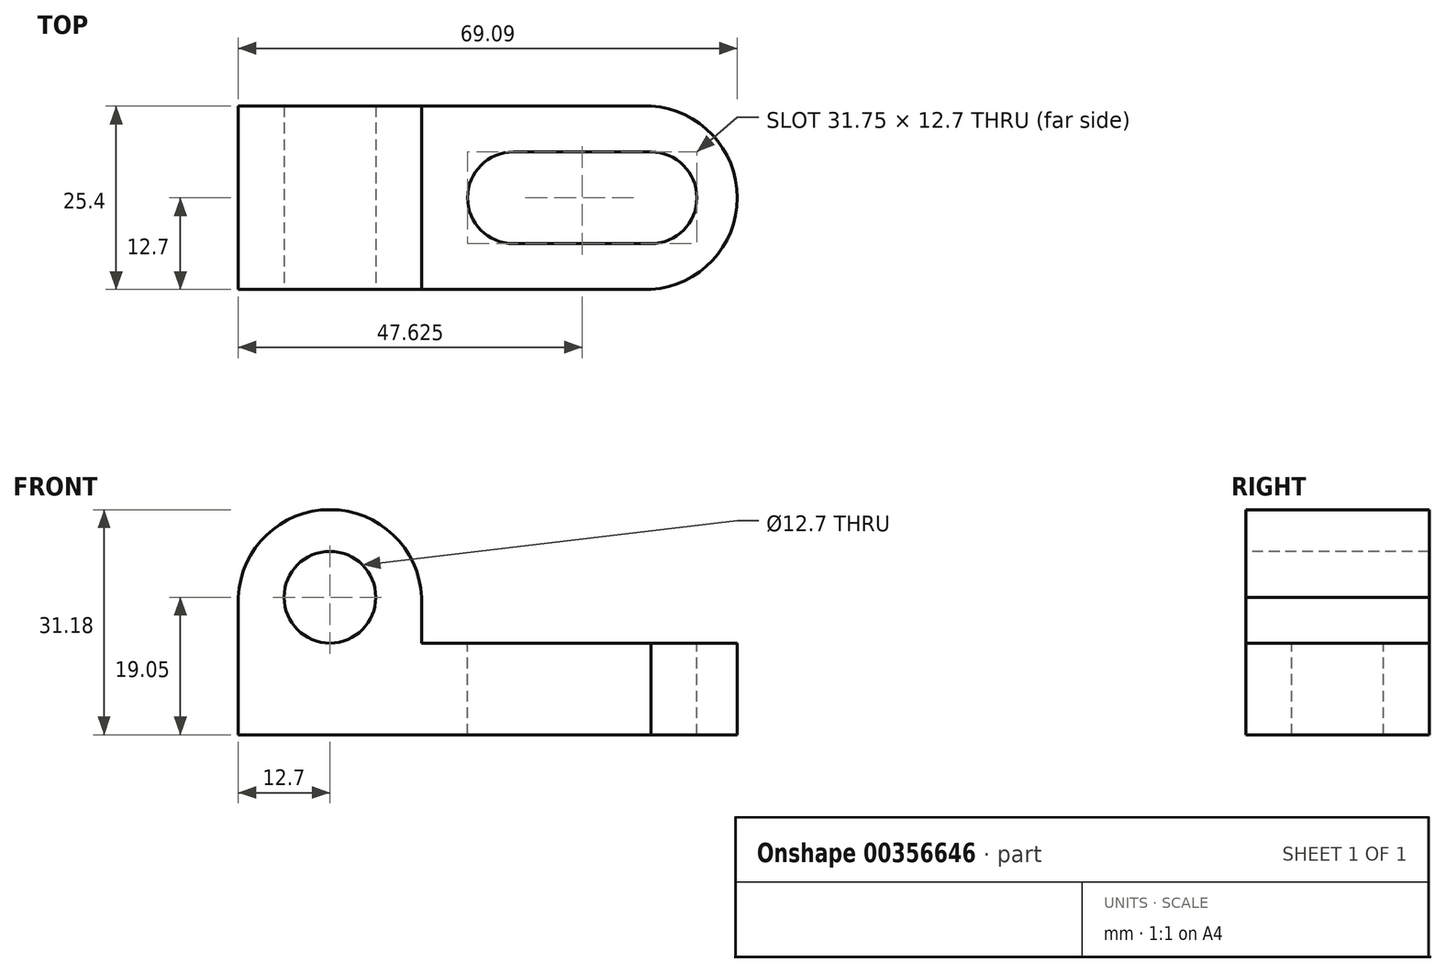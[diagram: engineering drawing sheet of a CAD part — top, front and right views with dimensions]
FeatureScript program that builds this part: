
annotation { "Feature Type Name" : "Feature", "Feature Type Description" : "" }
export const myFeature = defineFeature(function(context is Context, id is Id, definition is map)
    precondition{}
    {
        {
            var Q0;
            Q0=qCreatedBy(makeId("Front.planeOp"),FACE);
            var sketch = newSketch(context, id + "F0", { "sketchPlane" : qUnion([Q0])});
            skLineSegment(sketch, "E0", {"start": v(0, 0) * mm, "end": v(69.85, 0) * mm});
            skLineSegment(sketch, "E1", {"start": v(69.85, 0) * mm, "end": v(69.85, 12.7) * mm});
            skLineSegment(sketch, "E2", {"start": v(69.85, 12.7) * mm, "end": v(25.4, 12.7) * mm});
            skLineSegment(sketch, "E3", {"start": v(25.4, 12.7) * mm, "end": v(25.4, 31.75) * mm});
            skLineSegment(sketch, "E4", {"start": v(25.4, 31.75) * mm, "end": v(0, 31.75) * mm});
            skLineSegment(sketch, "E5", {"start": v(0, 31.75) * mm, "end": v(0, 0) * mm});
            skSolve(sketch);
        }
        {
            var Q0;
            Q0=makeQuery(id+"F0.imprint","IMPRINT",FACE,{"disambiguationData":[TD([[makeQuery(id+"F0.imprint","IMPRINT",EDGE,{"derivedFrom":sQuery(id+"F0.wireOp",EDGE,"E0")}),1.0]])]});
            extrude(context, id + "F1", {"entities" : qUnion([Q0]), "depth" : 25.4 * mm});
        }
        {
            var Q0;
            Q0=makeQuery(id+"F1.opExtrude","CAP_FACE",FACE,{"disambiguationData":[OSD([sQuery(id+"F0.wireOp",EDGE,"E0"),sQuery(id+"F0.wireOp",EDGE,"E1"),sQuery(id+"F0.wireOp",EDGE,"E2"),sQuery(id+"F0.wireOp",EDGE,"E3"),sQuery(id+"F0.wireOp",EDGE,"E4"),sQuery(id+"F0.wireOp",EDGE,"E5")])],"isStart":false});
            var sketch = newSketch(context, id + "F2", { "sketchPlane" : qUnion([Q0])});
            skCircle(sketch, "E6", {"center": v(12.7, 19.05) * mm, "radius": 6.35 * mm});
            skArc(sketch, "E7", {"start": v(25.4, 19.05) * mm, "mid": v(12.7, 31.18) * mm, "end": v(0, 19.05) * mm});
            skSolve(sketch);
        }
        {
            var Q0;
            {var subQ0=sQuery(id+"F2.wireOp",EDGE,"E7");Q0=makeQuery(id+"F2.imprint","IMPRINT",FACE,{"disambiguationData":[TD([[makeQuery(id+"F2.imprint","IMPRINT",EDGE,{"derivedFrom":subQ0}),-1.0]])]});}
            var Q1;
            Q1=makeQuery(id+"F2.imprint","IMPRINT",FACE,{"disambiguationData":[TD([[makeQuery(id+"F2.imprint","IMPRINT",EDGE,{"derivedFrom":sQuery(id+"F2.wireOp",EDGE,"E6")}),1.0]])]});
            extrude(context, id + "F3", {"entities" : qUnion([Q0, Q1]), "operationType" : NewBodyOperationType.REMOVE, "oppositeDirection" : true, "depth" : 25.4 * mm});
        }
        {
            var Q0;
            Q0=makeQuery(id+"F1.opExtrude","SWEPT_FACE",FACE,{"disambiguationData":[OSD([sQuery(id+"F0.wireOp",EDGE,"E2")])]});
            var sketch = newSketch(context, id + "F4", { "sketchPlane" : qUnion([Q0])});
            skCircle(sketch, "E8", {"center": v(38.1, -12.7) * mm, "radius": 6.35 * mm});
            skCircle(sketch, "E9", {"center": v(57.15, -12.7) * mm, "radius": 6.35 * mm});
            skLineSegment(sketch, "E10", {"start": v(38.1, -6.35) * mm, "end": v(57.15, -6.35) * mm});
            skLineSegment(sketch, "E11", {"start": v(38.1, -19.05) * mm, "end": v(57.15, -19.05) * mm});
            skArc(sketch, "E12", {"start": v(57.15, -25.4) * mm, "mid": v(69.09, -12.7) * mm, "end": v(57.15, 0) * mm});
            skSolve(sketch);
        }
        {
            var Q0;
            {var subQ0=sQuery(id+"F4.wireOp",EDGE,"E8");var subQ1=makeQuery(id+"F4.imprint","INTERSECT",VERTEX,{"derivedFrom":[subQ0,sQuery(id+"F4.wireOp",EDGE,"E10")]});Q0=makeQuery(id+"F4.imprint","IMPRINT",FACE,{"disambiguationData":[TD([[makeQuery(id+"F4.imprint","IMPRINT",EDGE,{"disambiguationData":[TD([[subQ1,-1.0]])],"derivedFrom":subQ0}),1.0]])]});}
            var Q1;
            {var subQ0=sQuery(id+"F4.wireOp",EDGE,"E10");Q1=makeQuery(id+"F4.imprint","IMPRINT",FACE,{"disambiguationData":[TD([[makeQuery(id+"F4.imprint","IMPRINT",EDGE,{"derivedFrom":subQ0}),-1.0]])]});}
            var Q2;
            {var subQ0=sQuery(id+"F4.wireOp",EDGE,"E9");var subQ1=makeQuery(id+"F4.imprint","INTERSECT",VERTEX,{"derivedFrom":[subQ0,sQuery(id+"F4.wireOp",EDGE,"E10")]});Q2=makeQuery(id+"F4.imprint","IMPRINT",FACE,{"disambiguationData":[TD([[makeQuery(id+"F4.imprint","IMPRINT",EDGE,{"disambiguationData":[TD([[subQ1,-1.0]])],"derivedFrom":subQ0}),1.0]])]});}
            var Q3;
            {var subQ0=sQuery(id+"F4.wireOp",EDGE,"E12");Q3=makeQuery(id+"F4.imprint","IMPRINT",FACE,{"disambiguationData":[TD([[makeQuery(id+"F4.imprint","IMPRINT",EDGE,{"derivedFrom":subQ0}),-1.0]])]});}
            extrude(context, id + "F5", {"entities" : qUnion([Q0, Q1, Q2, Q3]), "operationType" : NewBodyOperationType.REMOVE, "oppositeDirection" : true, "depth" : 25.4 * mm});
        }
    });
